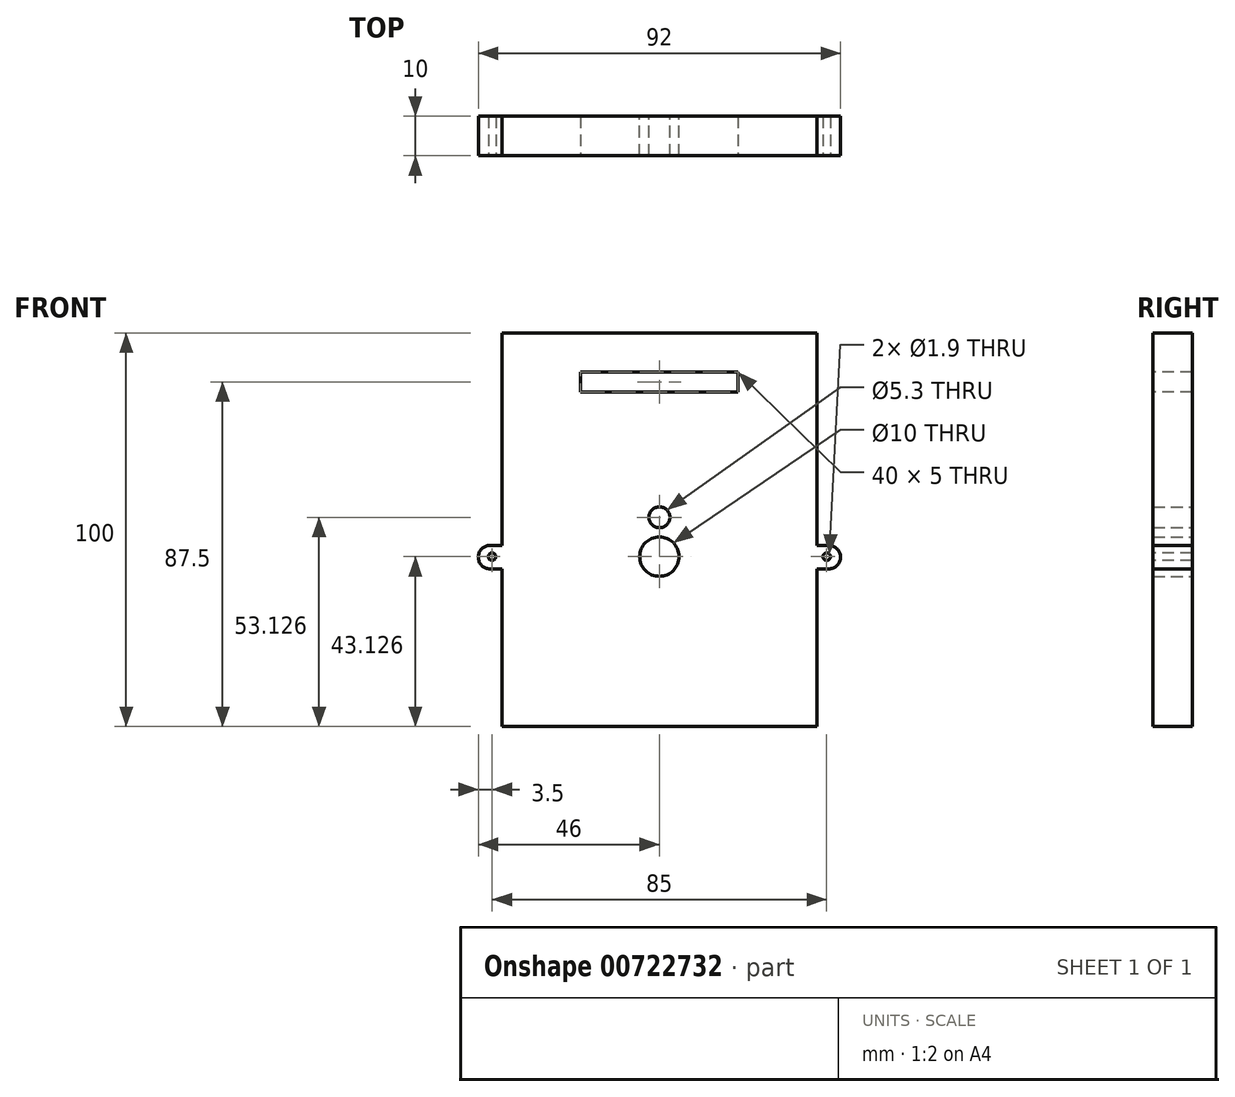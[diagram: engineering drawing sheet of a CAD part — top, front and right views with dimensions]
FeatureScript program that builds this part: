
annotation { "Feature Type Name" : "Feature", "Feature Type Description" : "" }
export const myFeature = defineFeature(function(context is Context, id is Id, definition is map)
    precondition{}
    {
        {
            var Q0;
            Q0=qCreatedBy(makeId("Front.planeOp"),FACE);
            var sketch = newSketch(context, id + "F0", { "sketchPlane" : qUnion([Q0])});
            skLineSegment(sketch, "E0.bottom", {"start": v(-40, 60) * mm, "end": v(40, 60) * mm});
            skLineSegment(sketch, "E0.top", {"start": v(-40, -60) * mm, "end": v(40, -60) * mm});
            skLineSegment(sketch, "E0.left", {"start": v(-40, 60) * mm, "end": v(-40, -60) * mm});
            skLineSegment(sketch, "E0.right", {"start": v(40, 60) * mm, "end": v(40, -60) * mm});
            skPoint(sketch, "E0.middle", {"position": v(0, 0) * mm});
            skLineSegment(sketch, "E1", {"start": v(0, 21.88) * mm, "end": v(0, 29.88) * mm, "construction": true});
            skLineSegment(sketch, "E2", {"start": v(0, 60) * mm, "end": v(0, 29.88) * mm, "construction": true});
            skLineSegment(sketch, "E3", {"start": v(0, 21.88) * mm, "end": v(0, 3.13) * mm, "construction": true});
            skLineSegment(sketch, "E4", {"start": v(0, 3.13) * mm, "end": v(0, 13.13) * mm, "construction": true});
            skCircle(sketch, "E5", {"center": v(0, 13.13) * mm, "radius": 2.65 * mm});
            skCircle(sketch, "E6", {"center": v(0, 3.13) * mm, "radius": 5 * mm});
            skSolve(sketch);
        }
        {
            var Q0;
            Q0=qSketchRegion(id+"F0",true);
            extrude(context, id + "F1", {"entities" : qUnion([Q0]), "depth" : 10 * mm, "offsetDistance" : 25 * mm, "symmetric" : true});
        }
        {
            var Q0;
            Q0=makeQuery(id+"F1.opExtrude","CAP_FACE",FACE,{"disambiguationData":[OSD([sQuery(id+"F0.wireOp",EDGE,"E0.bottom"),sQuery(id+"F0.wireOp",EDGE,"E0.top"),sQuery(id+"F0.wireOp",EDGE,"E0.left"),sQuery(id+"F0.wireOp",EDGE,"E0.right"),sQuery(id+"F0.wireOp",EDGE,"fTkhlyi4-ds1t-LeiX-dJr5-BQBYX8UqfuRu"),sQuery(id+"F0.wireOp",EDGE,"K3NiFW33-7Mkw-CSg8-gPCc-1bS3Ah0xoB45"),sQuery(id+"F0.wireOp",EDGE,"c0xHYhgZ-c2bo-p7RT-CEEI-62P9P62umUG7"),sQuery(id+"F0.wireOp",EDGE,"LGlnvPXJ-v3Kb-925D-2s2R-QpoeiBjVmgLV"),sQuery(id+"F0.wireOp",EDGE,"cU7F8PZ5-bHXt-zMFN-tRg9-2nZfbFJBMRA3")])],"isStart":false});
            var sketch = newSketch(context, id + "F2", { "sketchPlane" : qUnion([Q0])});
            skLineSegment(sketch, "E7.bottom", {"start": v(40, -60) * mm, "end": v(-40, -60) * mm});
            skLineSegment(sketch, "E7.top", {"start": v(40, -40) * mm, "end": v(-40, -40) * mm});
            skLineSegment(sketch, "E7.left", {"start": v(40, -60) * mm, "end": v(40, -40) * mm});
            skLineSegment(sketch, "E7.right", {"start": v(-40, -60) * mm, "end": v(-40, -40) * mm});
            skSolve(sketch);
        }
        {
            var Q0;
            Q0=qSketchRegion(id+"F2",true);
            extrude(context, id + "F3", {"entities" : qUnion([Q0]), "operationType" : NewBodyOperationType.REMOVE, "oppositeDirection" : true, "depth" : 10 * mm, "offsetDistance" : 25 * mm});
        }
        {
            var Q0;
            Q0=makeQuery(id+"F1.opExtrude","CAP_FACE",FACE,{"disambiguationData":[OSD([sQuery(id+"F0.wireOp",EDGE,"E0.bottom"),sQuery(id+"F0.wireOp",EDGE,"E0.top"),sQuery(id+"F0.wireOp",EDGE,"E0.left"),sQuery(id+"F0.wireOp",EDGE,"E0.right"),sQuery(id+"F0.wireOp",EDGE,"fTkhlyi4-ds1t-LeiX-dJr5-BQBYX8UqfuRu"),sQuery(id+"F0.wireOp",EDGE,"K3NiFW33-7Mkw-CSg8-gPCc-1bS3Ah0xoB45"),sQuery(id+"F0.wireOp",EDGE,"c0xHYhgZ-c2bo-p7RT-CEEI-62P9P62umUG7"),sQuery(id+"F0.wireOp",EDGE,"LGlnvPXJ-v3Kb-925D-2s2R-QpoeiBjVmgLV"),sQuery(id+"F0.wireOp",EDGE,"cU7F8PZ5-bHXt-zMFN-tRg9-2nZfbFJBMRA3")])],"isStart":false});
            var sketch = newSketch(context, id + "F4", { "sketchPlane" : qUnion([Q0])});
            skLineSegment(sketch, "E8", {"start": v(0, 3.13) * mm, "end": v(42.5, 3.13) * mm, "construction": true});
            skLineSegment(sketch, "E9", {"start": v(42.5, 3.13) * mm, "end": v(42.5, 0.13) * mm, "construction": true});
            skLineSegment(sketch, "E10.bottom", {"start": v(40, 0) * mm, "end": v(46, 0) * mm});
            skLineSegment(sketch, "E10.top", {"start": v(40, 6) * mm, "end": v(46, 6) * mm});
            skLineSegment(sketch, "E10.left", {"start": v(40, 0) * mm, "end": v(40, 6) * mm});
            skLineSegment(sketch, "E10.right", {"start": v(46, 0) * mm, "end": v(46, 6) * mm});
            skCircle(sketch, "E11", {"center": v(42.5, 3.13) * mm, "radius": 0.95 * mm});
            skSolve(sketch);
        }
        {
            var Q0;
            Q0=qSketchRegion(id+"F4",true);
            extrude(context, id + "F5", {"entities" : qUnion([Q0]), "oppositeDirection" : true, "depth" : 10 * mm, "offsetDistance" : 25 * mm});
        }
        {
            var Q0;
            Q0=makeQuery(id+"F5.opExtrude","SWEPT_EDGE",EDGE,{"disambiguationData":[OSD([sQuery(id+"F4.wireOp",EDGE,"E10.bottom"),sQuery(id+"F4.wireOp",EDGE,"E10.right")])]});
            var Q1;
            Q1=makeQuery(id+"F5.opExtrude","SWEPT_EDGE",EDGE,{"disambiguationData":[OSD([sQuery(id+"F4.wireOp",EDGE,"E10.top"),sQuery(id+"F4.wireOp",EDGE,"E10.right")])]});
            fillet(context, id + "F6", {"entities" : qUnion([Q0, Q1]), "radius" : 3 * mm, "tangentPropagation" : true, "allowEdgeOverflow" : false});
        }
        {
            var Q0;
            Q0=makeQuery(id+"F5.opExtrude","SWEPT_BODY",BODY,{"disambiguationData":[OSD([sQuery(id+"F4.wireOp",EDGE,"E10.bottom"),sQuery(id+"F4.wireOp",EDGE,"E10.top"),sQuery(id+"F4.wireOp",EDGE,"E10.left"),sQuery(id+"F4.wireOp",EDGE,"E10.right"),sQuery(id+"F4.wireOp",EDGE,"E11")])]});
            var Q1;
            Q1=qCreatedBy(makeId("Right.planeOp"),FACE);
            mirror(context, id + "F7", {"operationType" : NewBodyOperationType.ADD, "entities" : qUnion([Q0]), "mirrorPlane" : qUnion([Q1])});
        }
        {
            var Q0;
            Q0=makeQuery(id+"F1.opExtrude","CAP_FACE",FACE,{"disambiguationData":[OSD([sQuery(id+"F0.wireOp",EDGE,"E0.bottom"),sQuery(id+"F0.wireOp",EDGE,"E0.top"),sQuery(id+"F0.wireOp",EDGE,"E0.left"),sQuery(id+"F0.wireOp",EDGE,"E0.right"),sQuery(id+"F0.wireOp",EDGE,"BUhoPo5e-iJjO-Hz3U-B1AJ-PJeumMdkG3JQ"),sQuery(id+"F0.wireOp",EDGE,"rpFWY1n5-CffQ-x4gs-MNA2-rnEpYRzyCIXl"),sQuery(id+"F0.wireOp",EDGE,"iMyCUadU-kSq6-7gJk-bGzv-rUmCgOXwhL5P"),sQuery(id+"F0.wireOp",EDGE,"g6cQsEgE-VhaZ-rvnu-1JBG-t1yHCIxkASWM"),sQuery(id+"F0.wireOp",EDGE,"NTCEa5vw-s6QI-k5br-llQC-EMKQmXEYU9zL")])],"isStart":false});
            var sketch = newSketch(context, id + "F9", { "sketchPlane" : qUnion([Q0])});
            skLineSegment(sketch, "E12", {"start": v(40, 60) * mm, "end": v(20, 60) * mm, "construction": true});
            skLineSegment(sketch, "E13", {"start": v(20, 60) * mm, "end": v(20, 50) * mm, "construction": true});
            skLineSegment(sketch, "E14.bottom", {"start": v(20, 50) * mm, "end": v(-20, 50) * mm});
            skLineSegment(sketch, "E14.top", {"start": v(20, 45) * mm, "end": v(-20, 45) * mm});
            skLineSegment(sketch, "E14.left", {"start": v(20, 50) * mm, "end": v(20, 45) * mm});
            skLineSegment(sketch, "E14.right", {"start": v(-20, 50) * mm, "end": v(-20, 45) * mm});
            skSolve(sketch);
        }
        {
            var Q0;
            Q0=qSketchRegion(id+"F9",true);
            extrude(context, id + "F10", {"entities" : qUnion([Q0]), "operationType" : NewBodyOperationType.REMOVE, "oppositeDirection" : true, "depth" : 12 * mm, "offsetDistance" : 25 * mm, "hasSecondDirection" : true, "secondDirectionOppositeDirection" : false, "secondDirectionDepth" : 10 * mm});
        }
    });
